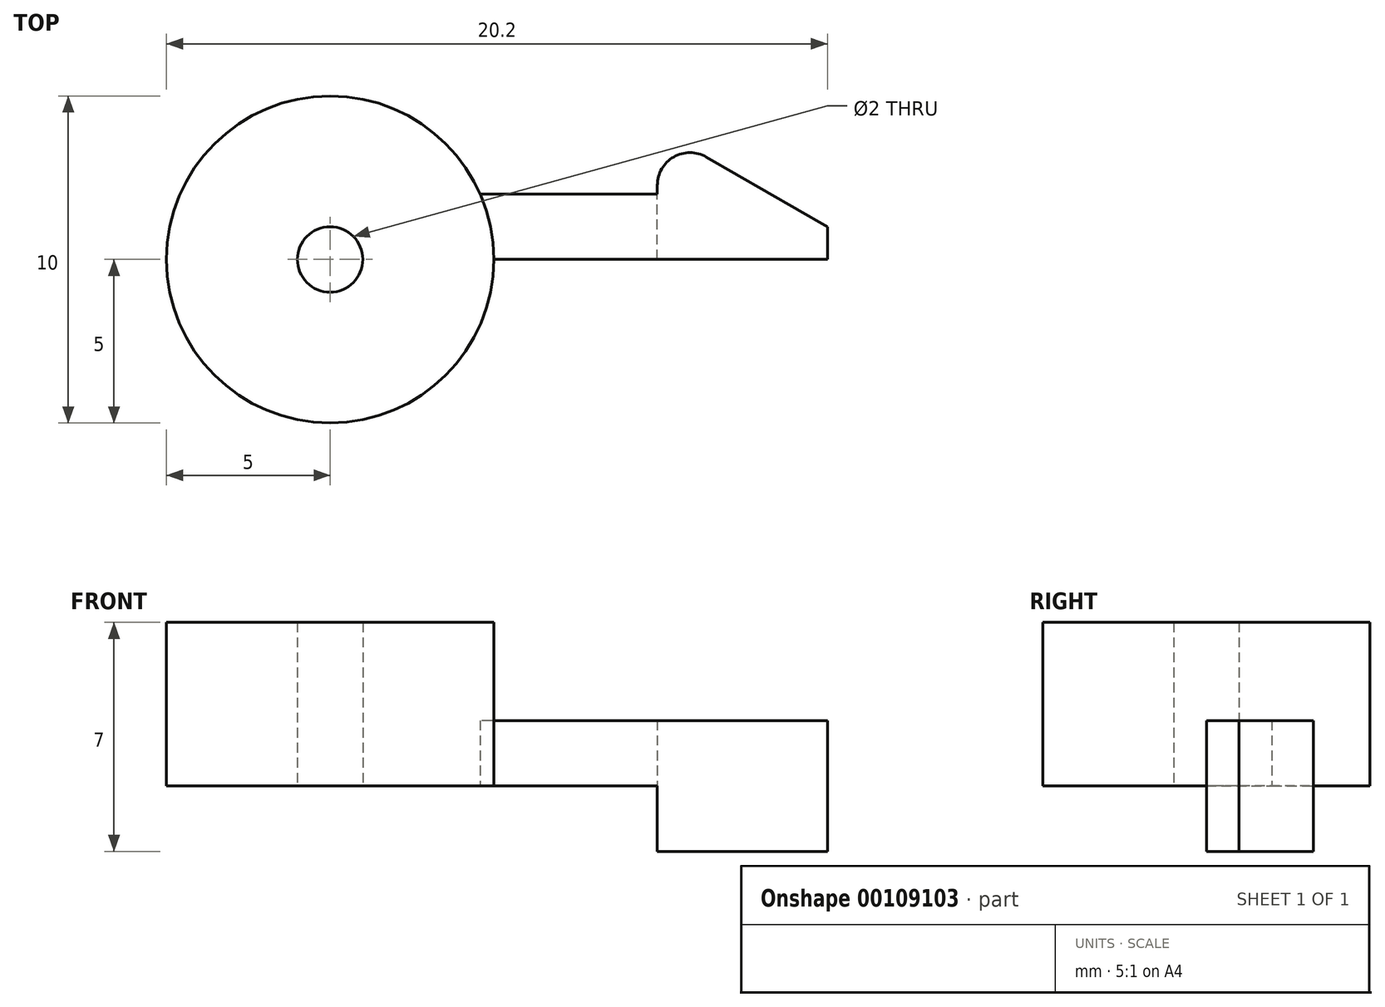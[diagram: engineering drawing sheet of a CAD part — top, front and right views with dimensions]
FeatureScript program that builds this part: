
annotation { "Feature Type Name" : "Feature", "Feature Type Description" : "" }
export const myFeature = defineFeature(function(context is Context, id is Id, definition is map)
    precondition{}
    {
        {
            var Q0;
            Q0=qCreatedBy(makeId("Top.planeOp"),FACE);
            var sketch = newSketch(context, id + "F0", { "sketchPlane" : qUnion([Q0])});
            skCircle(sketch, "E0", {"center": v(0, 0) * mm, "radius": 5 * mm});
            skLineSegment(sketch, "E1", {"start": v(10, 0) * mm, "end": v(10, 2) * mm});
            skLineSegment(sketch, "E2", {"start": v(10, 2) * mm, "end": v(4.58, 2) * mm});
            skLineSegment(sketch, "E3", {"start": v(10, 2) * mm, "end": v(10, 4) * mm});
            skLineSegment(sketch, "E4", {"start": v(10, 4) * mm, "end": v(15.2, 1) * mm});
            skLineSegment(sketch, "E5", {"start": v(15.2, 1) * mm, "end": v(15.2, 0) * mm});
            skLineSegment(sketch, "E6", {"start": v(15.2, 0) * mm, "end": v(5, 0) * mm});
            skSolve(sketch);
        }
        {
            var Q0;
            {var subQ0=sQuery(id+"F0.wireOp",EDGE,"E0");var subQ1=makeQuery(id+"F0.imprint","INTERSECT",VERTEX,{"derivedFrom":[subQ0,sQuery(id+"F0.wireOp",EDGE,"E2")]});Q0=makeQuery(id+"F0.imprint","IMPRINT",FACE,{"disambiguationData":[TD([[makeQuery(id+"F0.imprint","IMPRINT",EDGE,{"disambiguationData":[TD([[subQ1,1.0]])],"derivedFrom":subQ0}),1.0]])]});}
            extrude(context, id + "F1", {"entities" : qUnion([Q0]), "depth" : 5 * mm});
        }
        {
            var Q0;
            {var subQ4=sQuery(id+"F0.wireOp",EDGE,"E1");Q0=makeQuery(id+"F0.imprint","IMPRINT",FACE,{"disambiguationData":[TD([[makeQuery(id+"F0.imprint","IMPRINT",EDGE,{"derivedFrom":subQ4}),1.0]])]});}
            extrude(context, id + "F2", {"entities" : qUnion([Q0]), "operationType" : NewBodyOperationType.ADD, "depth" : 2 * mm});
        }
        {
            var Q0;
            {var subQ1=sQuery(id+"F0.wireOp",EDGE,"E1");Q0=makeQuery(id+"F0.imprint","IMPRINT",FACE,{"disambiguationData":[TD([[makeQuery(id+"F0.imprint","IMPRINT",EDGE,{"derivedFrom":subQ1}),-1.0]])]});}
            extrude(context, id + "F3", {"entities" : qUnion([Q0]), "operationType" : NewBodyOperationType.ADD, "endBound" : BoundingType.SYMMETRIC, "depth" : 4 * mm});
        }
        {
            var Q0;
            Q0=makeQuery(id+"F3.opExtrude","SWEPT_EDGE",EDGE,{"disambiguationData":[OSD([sQuery(id+"F0.wireOp",EDGE,"E3"),sQuery(id+"F0.wireOp",EDGE,"E4")])]});
            fillet(context, id + "F4", {"entities" : qUnion([Q0]), "radius" : 1 * mm, "tangentPropagation" : true, "allowEdgeOverflow" : false});
        }
        {
            var Q0;
            Q0=sQuery(id+"F0.wireOp",VERTEX,"E0.center");
            var Q1;
            Q1=makeQuery(id+"F1.opExtrude","SWEPT_BODY",BODY,{"disambiguationData":[OSD([sQuery(id+"F0.wireOp",EDGE,"E0")])]});
            hole(context, id + "F5", {"style" : HoleStyle.SIMPLE, "endStyle" : HoleEndStyle.THROUGH, "oppositeDirection" : true, "holeDiameter" : 2 * mm, "locations" : qUnion([Q0]), "scope" : qUnion([Q1]), "isTappedThrough" : true});
        }
    });
